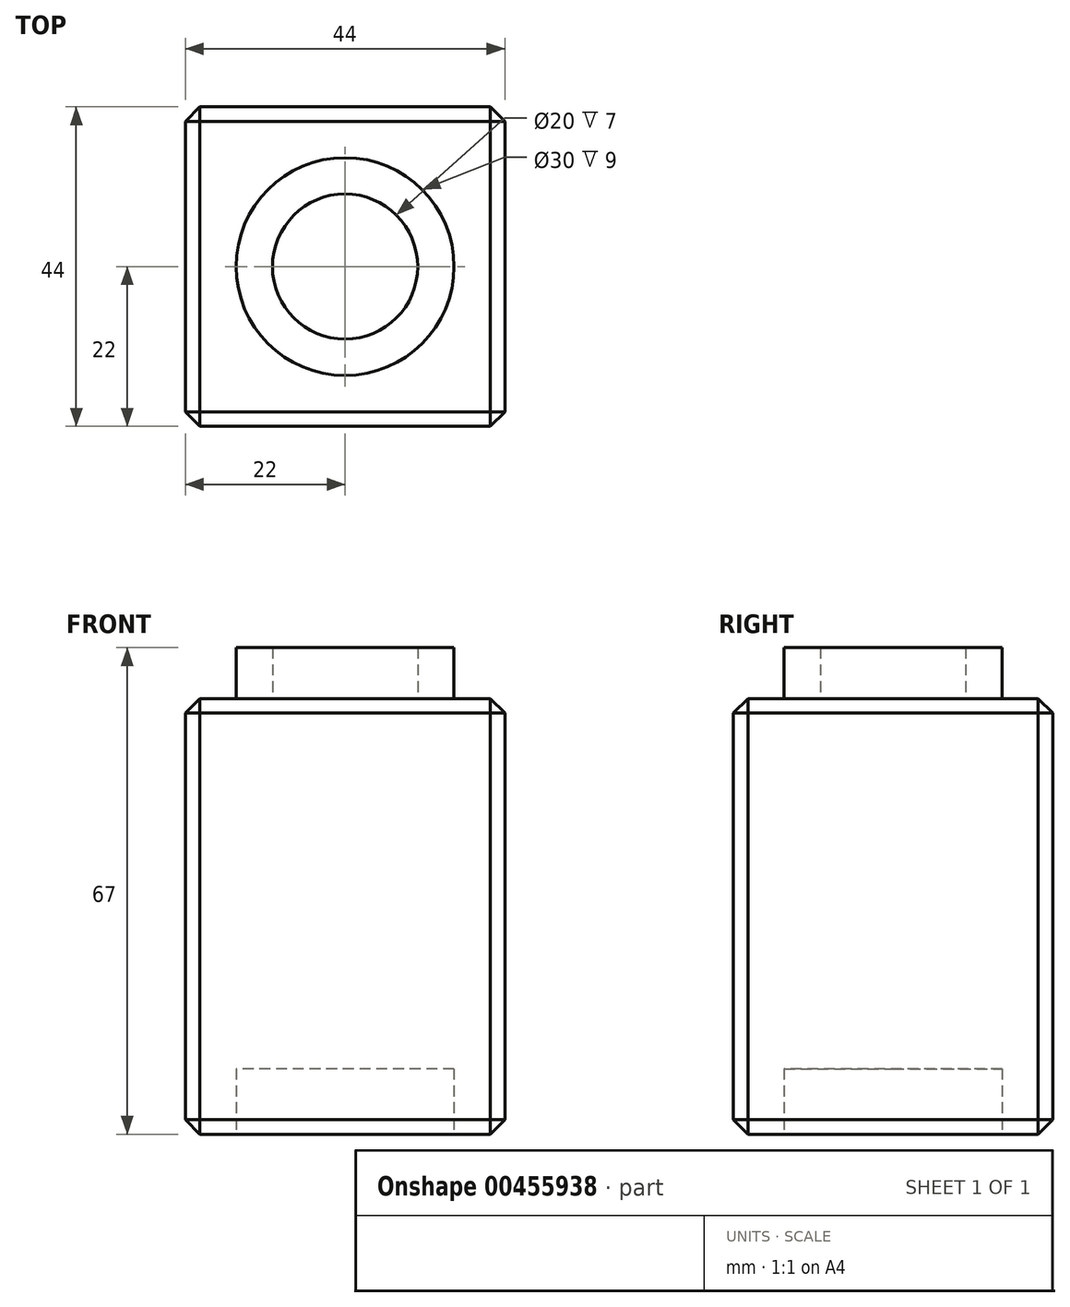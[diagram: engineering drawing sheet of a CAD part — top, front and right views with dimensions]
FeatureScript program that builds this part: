
annotation { "Feature Type Name" : "Feature", "Feature Type Description" : "" }
export const myFeature = defineFeature(function(context is Context, id is Id, definition is map)
    precondition{}
    {
        {
            assignVariable(context, id + "F0", {"name" : "H", "anyValue" : 60});
        }
        {
            assignVariable(context, id + "F1", {"name" : "h", "anyValue" : 7});
        }
        {
            var Q0;
            Q0=qCreatedBy(makeId("Top.planeOp"),FACE);
            var sketch = newSketch(context, id + "F2", { "sketchPlane" : qUnion([Q0])});
            skLineSegment(sketch, "E0.bottom", {"start": v(-22, 22) * mm, "end": v(22, 22) * mm});
            skLineSegment(sketch, "E0.top", {"start": v(-22, -22) * mm, "end": v(22, -22) * mm});
            skLineSegment(sketch, "E0.left", {"start": v(-22, 22) * mm, "end": v(-22, -22) * mm});
            skLineSegment(sketch, "E0.right", {"start": v(22, 22) * mm, "end": v(22, -22) * mm});
            skPoint(sketch, "E1", {"position": v(-22, 0) * mm});
            skPoint(sketch, "E2", {"position": v(0, 22) * mm});
            skCircle(sketch, "E3", {"center": v(0, 0) * mm, "radius": 15 * mm});
            skCircle(sketch, "E4", {"center": v(0, 0) * mm, "radius": 10 * mm});
            skSolve(sketch);
        }
        {
            var Q0;
            Q0=makeQuery(id+"F2.imprint","IMPRINT",FACE,{"disambiguationData":[TD([[makeQuery(id+"F2.imprint","IMPRINT",EDGE,{"derivedFrom":sQuery(id+"F2.wireOp",EDGE,"E0.bottom")}),-1.0]])]});
            var Q1;
            Q1=makeQuery(id+"F2.imprint","IMPRINT",FACE,{"disambiguationData":[TD([[makeQuery(id+"F2.imprint","IMPRINT",EDGE,{"derivedFrom":sQuery(id+"F2.wireOp",EDGE,"E3")}),1.0]])]});
            var Q2;
            Q2=makeQuery(id+"F2.imprint","IMPRINT",FACE,{"disambiguationData":[TD([[makeQuery(id+"F2.imprint","IMPRINT",EDGE,{"derivedFrom":sQuery(id+"F2.wireOp",EDGE,"E4")}),1.0]])]});
            extrude(context, id + "F3", {"entities" : qUnion([Q0, Q1, Q2]), "depth" : (getVariable(context, 'H')) * mm});
        }
        {
            var Q0;
            Q0=makeQuery(id+"F3.opExtrude","CAP_FACE",FACE,{"disambiguationData":[OSD([sQuery(id+"F2.wireOp",EDGE,"E0.bottom"),sQuery(id+"F2.wireOp",EDGE,"E0.top"),sQuery(id+"F2.wireOp",EDGE,"E0.left"),sQuery(id+"F2.wireOp",EDGE,"E0.right")])],"isStart":false});
            var sketch = newSketch(context, id + "F4", { "sketchPlane" : qUnion([Q0])});
            skLineSegment(sketch, "E5.bottom", {"start": v(-22, 22) * mm, "end": v(22, 22) * mm});
            skLineSegment(sketch, "E5.top", {"start": v(-22, -22) * mm, "end": v(22, -22) * mm});
            skLineSegment(sketch, "E5.left", {"start": v(-22, 22) * mm, "end": v(-22, -22) * mm});
            skLineSegment(sketch, "E5.right", {"start": v(22, 22) * mm, "end": v(22, -22) * mm});
            skPoint(sketch, "E6", {"position": v(-22, 0) * mm});
            skPoint(sketch, "E7", {"position": v(0, 22) * mm});
            skCircle(sketch, "E8", {"center": v(0, 0) * mm, "radius": 15 * mm});
            skCircle(sketch, "E9", {"center": v(0, 0) * mm, "radius": 10 * mm});
            skSolve(sketch);
        }
        {
            var Q0;
            Q0=makeQuery(id+"F4.imprint","IMPRINT",FACE,{"disambiguationData":[TD([[makeQuery(id+"F4.imprint","IMPRINT",EDGE,{"derivedFrom":sQuery(id+"F4.wireOp",EDGE,"E8")}),1.0]])]});
            extrude(context, id + "F5", {"entities" : qUnion([Q0]), "operationType" : NewBodyOperationType.ADD, "depth" : (getVariable(context, 'h')) * mm});
        }
        {
            var Q0;
            Q0=makeQuery(id+"F2.imprint","IMPRINT",FACE,{"disambiguationData":[TD([[makeQuery(id+"F2.imprint","IMPRINT",EDGE,{"derivedFrom":sQuery(id+"F2.wireOp",EDGE,"E3")}),1.0]])]});
            var Q1;
            Q1=makeQuery(id+"F2.imprint","IMPRINT",FACE,{"disambiguationData":[TD([[makeQuery(id+"F2.imprint","IMPRINT",EDGE,{"derivedFrom":sQuery(id+"F2.wireOp",EDGE,"E4")}),1.0]])]});
            extrude(context, id + "F6", {"entities" : qUnion([Q0, Q1]), "operationType" : NewBodyOperationType.REMOVE, "depth" : (getVariable(context, 'h') + 2) * mm});
        }
        {
            assignVariable(context, id + "F7", {"name" : "c", "anyValue" : 2});
        }
        {
            var Q0;
            Q0=makeQuery(id+"F3.opExtrude","CAP_EDGE",EDGE,{"disambiguationData":[OSD([sQuery(id+"F2.wireOp",EDGE,"E0.top")])],"isStart":true});
            var Q1;
            Q1=makeQuery(id+"F3.opExtrude","CAP_EDGE",EDGE,{"disambiguationData":[OSD([sQuery(id+"F2.wireOp",EDGE,"E0.right")])],"isStart":true});
            var Q2;
            Q2=makeQuery(id+"F3.opExtrude","CAP_EDGE",EDGE,{"disambiguationData":[OSD([sQuery(id+"F2.wireOp",EDGE,"E0.left")])],"isStart":true});
            var Q3;
            Q3=makeQuery(id+"F3.opExtrude","CAP_EDGE",EDGE,{"disambiguationData":[OSD([sQuery(id+"F2.wireOp",EDGE,"E0.bottom")])],"isStart":true});
            var Q4;
            Q4=makeQuery(id+"F3.opExtrude","SWEPT_EDGE",EDGE,{"disambiguationData":[OSD([sQuery(id+"F2.wireOp",EDGE,"E0.top"),sQuery(id+"F2.wireOp",EDGE,"E0.left")])]});
            var Q5;
            Q5=makeQuery(id+"F3.opExtrude","SWEPT_EDGE",EDGE,{"disambiguationData":[OSD([sQuery(id+"F2.wireOp",EDGE,"E0.bottom"),sQuery(id+"F2.wireOp",EDGE,"E0.left")])]});
            var Q6;
            Q6=makeQuery(id+"F3.opExtrude","SWEPT_EDGE",EDGE,{"disambiguationData":[OSD([sQuery(id+"F2.wireOp",EDGE,"E0.bottom"),sQuery(id+"F2.wireOp",EDGE,"E0.right")])]});
            var Q7;
            Q7=makeQuery(id+"F3.opExtrude","SWEPT_EDGE",EDGE,{"disambiguationData":[OSD([sQuery(id+"F2.wireOp",EDGE,"E0.top"),sQuery(id+"F2.wireOp",EDGE,"E0.right")])]});
            var Q8;
            Q8=makeQuery(id+"F3.opExtrude","CAP_EDGE",EDGE,{"disambiguationData":[OSD([sQuery(id+"F2.wireOp",EDGE,"E0.right")])],"isStart":false});
            var Q9;
            Q9=makeQuery(id+"F3.opExtrude","CAP_EDGE",EDGE,{"disambiguationData":[OSD([sQuery(id+"F2.wireOp",EDGE,"E0.top")])],"isStart":false});
            var Q10;
            Q10=makeQuery(id+"F3.opExtrude","CAP_EDGE",EDGE,{"disambiguationData":[OSD([sQuery(id+"F2.wireOp",EDGE,"E0.left")])],"isStart":false});
            var Q11;
            Q11=makeQuery(id+"F3.opExtrude","CAP_EDGE",EDGE,{"disambiguationData":[OSD([sQuery(id+"F2.wireOp",EDGE,"E0.bottom")])],"isStart":false});
            var Q12;
            Q12=makeQuery(id+"F6.boolean.opBoolean","COPY",EDGE,{"derivedFrom":makeQuery(id+"F6.opExtrude","CAP_EDGE",EDGE,{"disambiguationData":[OSD([sQuery(id+"F2.wireOp",EDGE,"E3")])],"isStart":true})});
            chamfer(context, id + "F8", {"entities" : qUnion([Q0, Q1, Q2, Q3, Q4, Q5, Q6, Q7, Q8, Q9, Q10, Q11, Q12]), "width" : (getVariable(context, 'c')) * mm, "tangentPropagation" : true});
        }
    });
